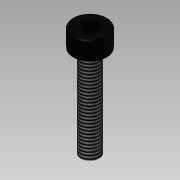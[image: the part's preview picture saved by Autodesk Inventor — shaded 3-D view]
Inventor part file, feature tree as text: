
AUTODESK INVENTOR PART (.ipt)
format: ipt  version: 2014 (Build 180170000, 170)  size: 112,640 bytes
history: native  units: mm
features: extrude x4, sketch x4, fillet x1, thread x1, reference x1
ambient origin geometry x8: Origin, YZ Plane, XZ Plane, XY Plane, X Axis, Y Axis, Z Axis, Center Point
bodies: Solid1 (feature_tree)
feature tree (11):
  extrude  "Extrusion1"  Depth=15.0mm TaperAngle=0.0deg
  extrude  "Extrusion2"  Depth=3.0mm TaperAngle=0.0deg
  fillet  "Fillet1"  Radius=0.3mm
  extrude  "Extrusion3"  Depth=0.5mm TaperAngle=0.0deg
  extrude  "Extrusion4"  Depth=2.0mm TaperAngle=0.0deg
  thread  "Thread1"  [1 undecoded]
  sketch  "Sketch1"  dims[d0=3.0mm d1=15.0mm d2=0.0mm]
  reference  "Reference1"
  sketch  "Sketch2"  dims[d3=5.6mm d4=3.0mm d5=0.0mm d6=0.3mm]
  sketch  "Sketch3"  dims[d7=5.5mm d8=0.5mm d9=0.0mm]
  sketch  "Sketch4"  dims[d10=2.5mm d11=2.0mm d12=0.0mm d13=10.0mm d14=0.0mm]
note: 1 required parameter value undecoded (feature->parameter linkage not recoverable at this tier; creation-order binding heuristic only, values carry confidence <= 0.55)
